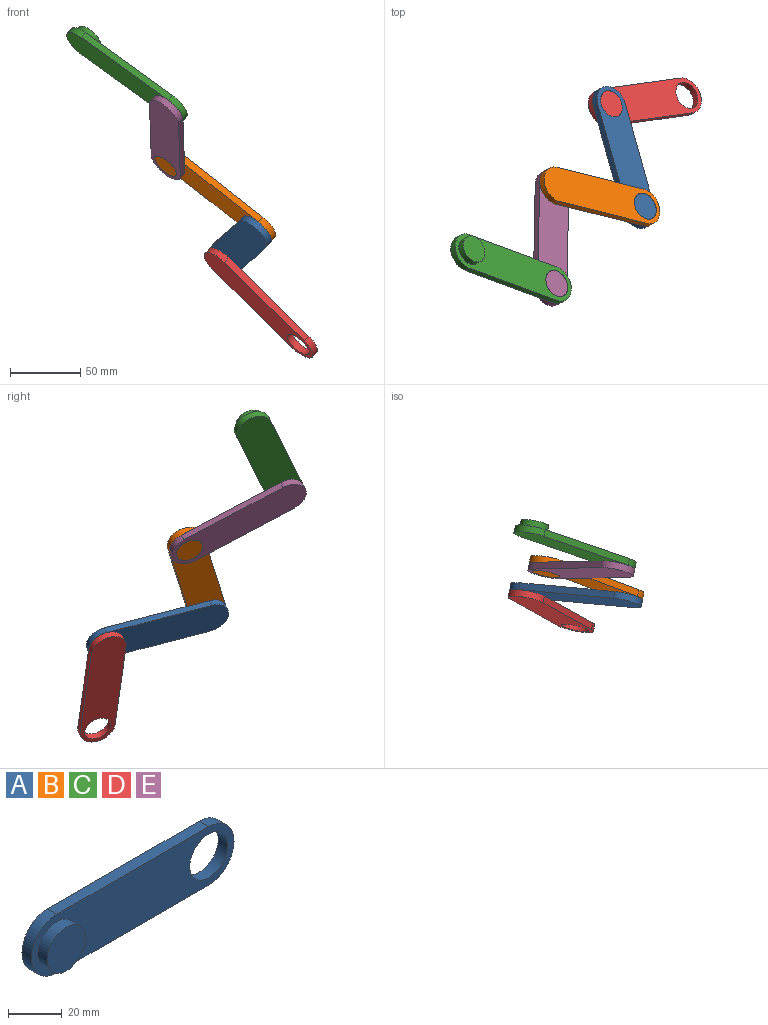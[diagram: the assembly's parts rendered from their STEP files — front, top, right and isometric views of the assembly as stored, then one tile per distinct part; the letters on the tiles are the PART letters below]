
ASSEMBLY  parts=5 mates=4
PART A: 9 faces, bbox 106.7x10x26.7 mm
  f0: cylinder r=13.33mm len=26.67mm, axis (0,1,0), area 209.4mm2, adj f1,f3,f4,f5
  f1: plane 80x5mm, normal (0,0,-1), area 400mm2, adj f0,f2,f4,f5
  f2: cylinder r=13.33mm len=26.67mm, axis (0,1,0), area 209.4mm2, adj f1,f3,f4,f5
  f3: plane 80x5mm, normal (0,0,1), area 400mm2, adj f0,f2,f4,f5
  f4: plane 106.67x26.67mm, normal (0,-1,0), area 2063.5mm2, adj f0,f1,f2,f3,f6,f8
  f5: plane 106.67x26.67mm, normal (0,1,0), area 2377.7mm2, adj f0,f1,f2,f3,f8
  f6: cylinder r=10mm len=20mm, axis (0,1,0), area 314.2mm2, adj f4,f7
  f7: plane 20x20mm, normal (0,-1,0), area 314.2mm2, adj f6
  f8: cylinder r=10mm len=20mm, axis (0,-1,0), area 314.2mm2, adj f4,f5
PART B: same geometry as A
PART C: same geometry as A
PART D: same geometry as A
PART E: same geometry as A
PLACE A rot(axis=(-0.37,-0.28,0.88),117.8deg) t=(30.36,304.13,17.81)mm
PLACE B rot(axis=(0.83,0.36,-0.43),74.9deg) t=(47.04,244.38,47.73)mm
PLACE C rot(axis=(-0.92,0.33,0.2),121.1deg) t=(-16.43,127.99,158.04)mm
PLACE D rot(axis=(-0.89,0.21,0.4),114.7deg) t=(85.26,266.87,-20.37)mm
PLACE E rot(axis=(-0.54,-0.17,0.82),113.2deg) t=(-4.91,233.27,86.31)mm
MATE revolute E.f2 <-> B.f0  axis (-0.63,-0.35,-0.69) through (-30.05,229.78,111.02)mm
MATE revolute B.f2 <-> A.f0  axis (0.63,0.35,0.69) through (38.03,217.92,69.5)mm
MATE revolute A.f2 <-> D.f0  axis (-0.63,-0.35,-0.69) through (13.99,290.92,46.75)mm
MATE revolute C.f2 <-> E.f0  axis (0.63,0.35,0.69) through (-25.02,162.62,155.35)mm
